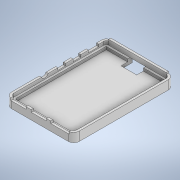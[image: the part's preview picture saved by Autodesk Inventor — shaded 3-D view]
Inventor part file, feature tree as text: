
AUTODESK INVENTOR PART (.ipt)
format: ipt  version: 2022 (Build 260153000, 153)  size: 256,000 bytes
history: native  units: in
note: dims shown in document units (in); Inventor stores cm internally (conversion verified against a paired STEP export)
features: extrude x7, sketch x7
ambient origin geometry x8: Origin, YZ Plane, XZ Plane, XY Plane, X Axis, Y Axis, Z Axis, Center Point
bodies: Solid1 (feature_tree)
feature tree (14):
  extrude  "Extrusion1"  Depth=3.3661in
  extrude  "Extrusion2"  Depth=0.1181in
  extrude  "Extrusion3"  Depth=0.1181in TaperAngle=0.0deg
  extrude  "Extrusion4"  Depth=0.0591in
  extrude  "Extrusion5"  Depth=0.1575in
  extrude  "Extrusion6"  Depth=0.5512in
  extrude  "Extrusion7"  Depth=0.1969in
  sketch  "Sketch1"  dims[d0=2.2244in d1=3.3661in]
  sketch  "Sketch2"  dims[d2=0.0787in d3=0.1181in]
  sketch  "Sketch3"  dims[d4=0.0787in d5=0.1181in d6=0.0in]
  sketch  "Sketch4"  dims[d7=0.0984in d8=0.0in d9=0.0591in]
  sketch  "Sketch5"  dims[d10=0.0787in d11=0.0in d12=0.1575in]
  sketch  "Sketch6"  dims[d13=0.0984in d14=0.0in d16=0.5512in]
  sketch  "Sketch7"  dims[d17=0.0in d18=0.1969in d19=0.3937in d20=0.0in d21=0.2626in d22=0.3619in d23=0.8964in d25=0.2665in d26=0.2665in d27=1.431in d28=2.0399in d29=0.2362in d30=0.0787in d31=0.3937in d32=0.0in d33=0.0787in d34=0.0898in d35=0.5354in d36=0.8048in d37=0.5354in d38=1.4952in d39=0.6442in d40=0.1969in d41=0.0in]
